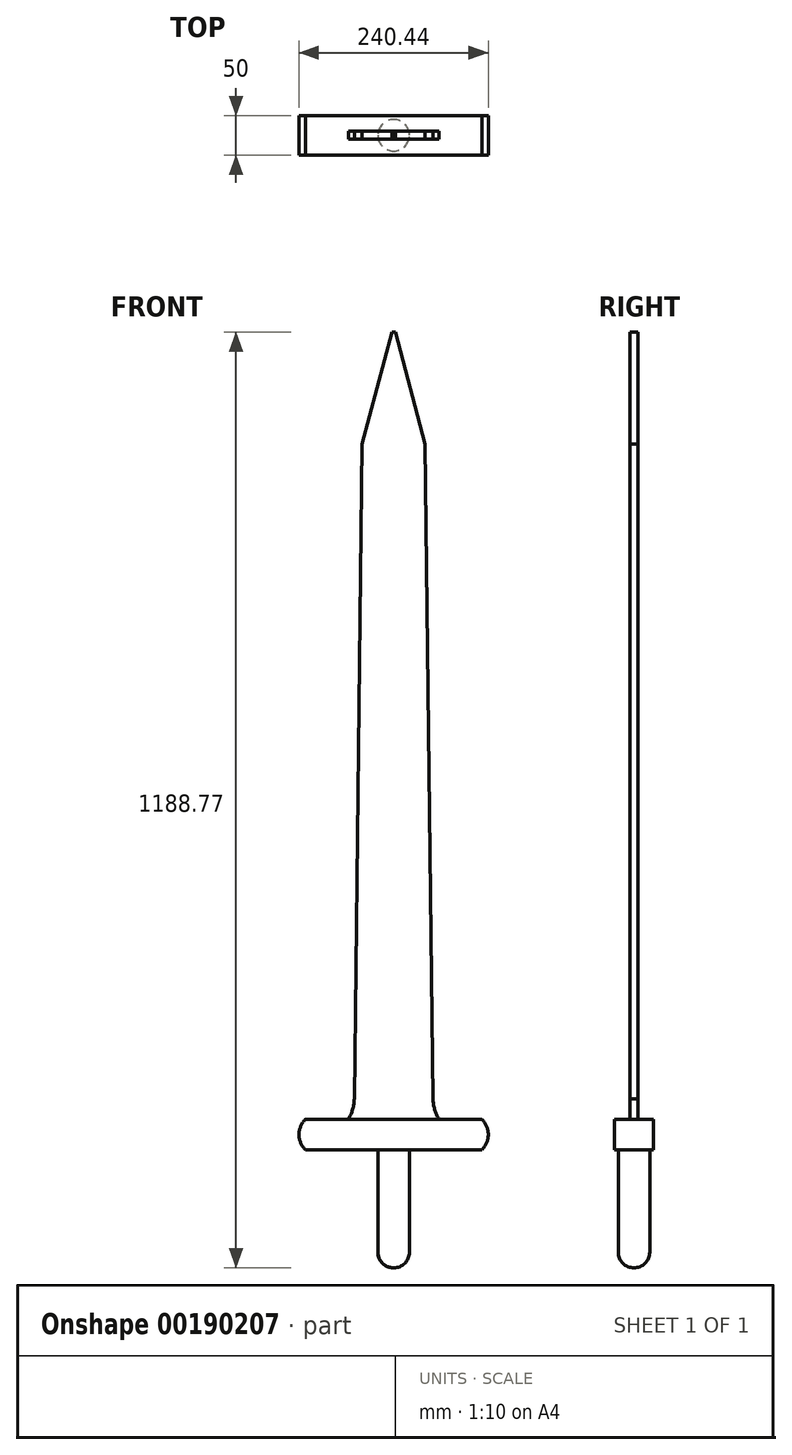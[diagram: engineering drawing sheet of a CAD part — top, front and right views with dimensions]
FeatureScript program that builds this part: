
annotation { "Feature Type Name" : "Feature", "Feature Type Description" : "" }
export const myFeature = defineFeature(function(context is Context, id is Id, definition is map)
    precondition{}
    {
        {
            var Q0;
            Q0=qCreatedBy(makeId("Front.planeOp"),FACE);
            var sketch = newSketch(context, id + "F0", { "sketchPlane" : qUnion([Q0])});
            skLineSegment(sketch, "E0", {"start": v(0, 0) * mm, "end": v(0, 1000) * mm, "construction": true});
            skLineSegment(sketch, "E1", {"start": v(-2, 1000) * mm, "end": v(-40, 857.6) * mm});
            skLineSegment(sketch, "E2", {"start": v(-40, 857.6) * mm, "end": v(-50, 26.19) * mm});
            skLineSegment(sketch, "E3", {"start": v(0, 0) * mm, "end": v(-60, 0) * mm});
            skArc(sketch, "E4", {"start": v(-57.56, 0) * mm, "mid": v(-52.11, 12.61) * mm, "end": v(-50, 26.19) * mm});
            skLineSegment(sketch, "E5.MirrorCS", {"start": v(2, 1000) * mm, "end": v(40, 857.6) * mm});
            skLineSegment(sketch, "E6.MirrorCS", {"start": v(40, 857.6) * mm, "end": v(50, 26.19) * mm});
            skArc(sketch, "E7.MirrorCS", {"start": v(57.56, 0) * mm, "mid": v(52.11, 12.61) * mm, "end": v(50, 26.19) * mm});
            skLineSegment(sketch, "E8", {"start": v(-2, 1000) * mm, "end": v(2, 1000) * mm});
            skLineSegment(sketch, "E9.MirrorCS", {"start": v(0, 0) * mm, "end": v(60, 0) * mm});
            skLineSegment(sketch, "E10", {"start": v(-57.56, 0) * mm, "end": v(-112.02, 0) * mm});
            skLineSegment(sketch, "E11", {"start": v(-112.02, -38.77) * mm, "end": v(0, -38.77) * mm});
            skArc(sketch, "E12", {"start": v(-112.02, 0) * mm, "mid": v(-120.22, -19.38) * mm, "end": v(-112.02, -38.77) * mm});
            skArc(sketch, "E13.MirrorCS", {"start": v(112.02, 0) * mm, "mid": v(120.22, -19.38) * mm, "end": v(112.02, -38.77) * mm});
            skLineSegment(sketch, "E14.MirrorCS", {"start": v(112.02, -38.77) * mm, "end": v(0, -38.77) * mm});
            skLineSegment(sketch, "E15.MirrorCS", {"start": v(57.56, 0) * mm, "end": v(112.02, 0) * mm});
            skSolve(sketch);
        }
        {
            var Q0;
            Q0=makeQuery(id+"F0.imprint","IMPRINT",FACE,{"disambiguationData":[TD([[makeQuery(id+"F0.imprint","IMPRINT",EDGE,{"derivedFrom":sQuery(id+"F0.wireOp",EDGE,"E1")}),1.0]])]});
            extrude(context, id + "F1", {"entities" : qUnion([Q0]), "endBound" : BoundingType.SYMMETRIC, "depth" : 10 * mm});
        }
        {
            var Q0;
            {var subQ1=sQuery(id+"F0.wireOp",EDGE,"E3");Q0=makeQuery(id+"F0.imprint","IMPRINT",FACE,{"disambiguationData":[TD([[makeQuery(id+"F0.imprint","IMPRINT",EDGE,{"derivedFrom":subQ1}),1.0]])]});}
            extrude(context, id + "F2", {"entities" : qUnion([Q0]), "endBound" : BoundingType.SYMMETRIC, "depth" : 50 * mm});
        }
        {
            var Q0;
            Q0=makeQuery(id+"F2.opExtrude","SWEPT_FACE",FACE,{"disambiguationData":[OSD([sQuery(id+"F0.wireOp",EDGE,"E11"),sQuery(id+"F0.wireOp",EDGE,"E14.MirrorCS")])]});
            var sketch = newSketch(context, id + "F3", { "sketchPlane" : qUnion([Q0])});
            skCircle(sketch, "E16", {"center": v(0, 0) * mm, "radius": 20 * mm});
            skSolve(sketch);
        }
        {
            var Q0;
            Q0 = qSketchRegion(id + "F3", true);
            extrude(context, id + "F4", {"entities" : qUnion([Q0]), "depth" : 150 * mm});
        }
        {
            var Q0;
            Q0=makeQuery(id+"F4.opExtrude","CAP_FACE",FACE,{"disambiguationData":[OSD([sQuery(id+"F3.wireOp",EDGE,"E16")])],"isStart":false});
            fillet(context, id + "F5", {"entities" : qUnion([Q0]), "radius" : 20 * mm, "tangentPropagation" : true, "allowEdgeOverflow" : false});
        }
    });
